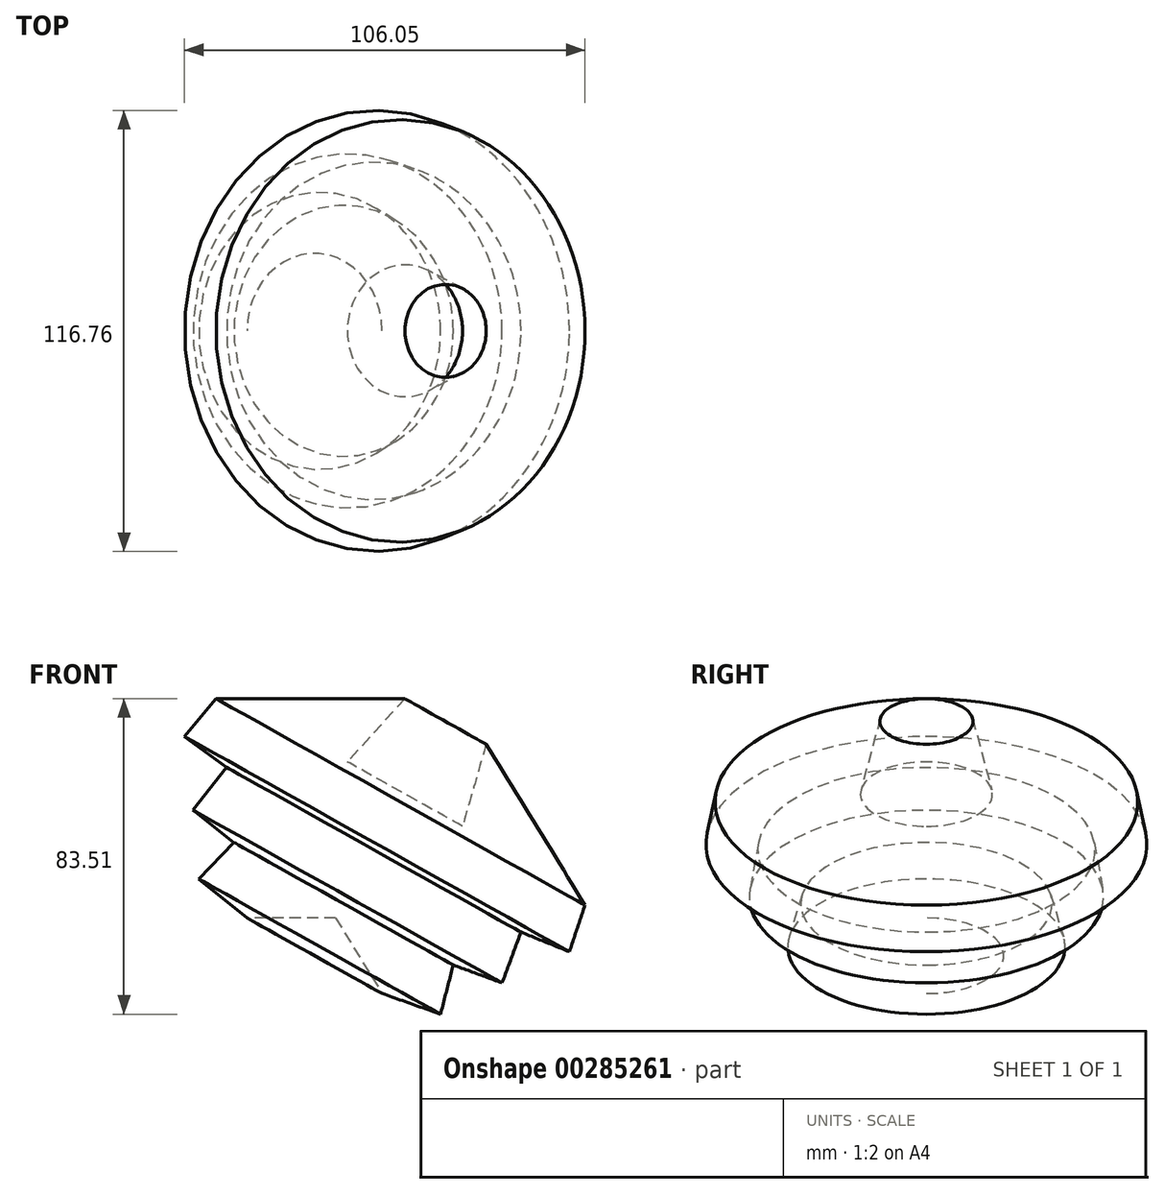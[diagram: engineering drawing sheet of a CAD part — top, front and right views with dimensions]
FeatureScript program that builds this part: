
annotation { "Feature Type Name" : "Feature", "Feature Type Description" : "" }
export const myFeature = defineFeature(function(context is Context, id is Id, definition is map)
    precondition{}
    {
        {
            var Q0;
            Q0=qCreatedBy(makeId("Front.planeOp"),FACE);
            var sketch = newSketch(context, id + "F0", { "sketchPlane" : qUnion([Q0])});
            skLineSegment(sketch, "E0", {"start": v(-41.8, 0) * mm, "end": v(0, 0) * mm});
            skLineSegment(sketch, "E1", {"start": v(0, 0) * mm, "end": v(-41.8, 0) * mm});
            skLineSegment(sketch, "E2", {"start": v(-54.6, 10.33) * mm, "end": v(-41.8, 0) * mm});
            skLineSegment(sketch, "E3", {"start": v(-45.25, 20) * mm, "end": v(-54.6, 10.33) * mm});
            skLineSegment(sketch, "E4", {"start": v(-56.07, 28.52) * mm, "end": v(-45.25, 20) * mm});
            skLineSegment(sketch, "E5", {"start": v(-47.21, 39.84) * mm, "end": v(-56.07, 28.52) * mm});
            skLineSegment(sketch, "E6", {"start": v(-58.36, 48.03) * mm, "end": v(-47.21, 39.84) * mm});
            skLineSegment(sketch, "E7", {"start": v(-50, 58.03) * mm, "end": v(-58.36, 48.03) * mm});
            skLineSegment(sketch, "E8", {"start": v(0, 58.03) * mm, "end": v(-50, 58.03) * mm});
            skLineSegment(sketch, "E9", {"start": v(-15.25, 41.31) * mm, "end": v(0, 58.03) * mm});
            skLineSegment(sketch, "E10", {"start": v(-15.25, 41.31) * mm, "end": v(0, 32.79) * mm});
            skLineSegment(sketch, "E11", {"start": v(0, 32.79) * mm, "end": v(-18.33, 0) * mm});
            skSolve(sketch);
        }
        {
            var Q0;
            {var subQ0=sQuery(id+"F0.wireOp",EDGE,"E2");Q0=makeQuery(id+"F0.imprint","IMPRINT",FACE,{"disambiguationData":[TD([[makeQuery(id+"F0.imprint","IMPRINT",EDGE,{"derivedFrom":subQ0}),1.0]])]});}
            var Q1;
            Q1=sQuery(id+"F0.wireOp",EDGE,"E11");
            revolve(context, id + "F1", {"entities" : qUnion([Q0]), "axis" : qUnion([Q1]), "revolveType" : RevolveType.FULL});
        }
    });
